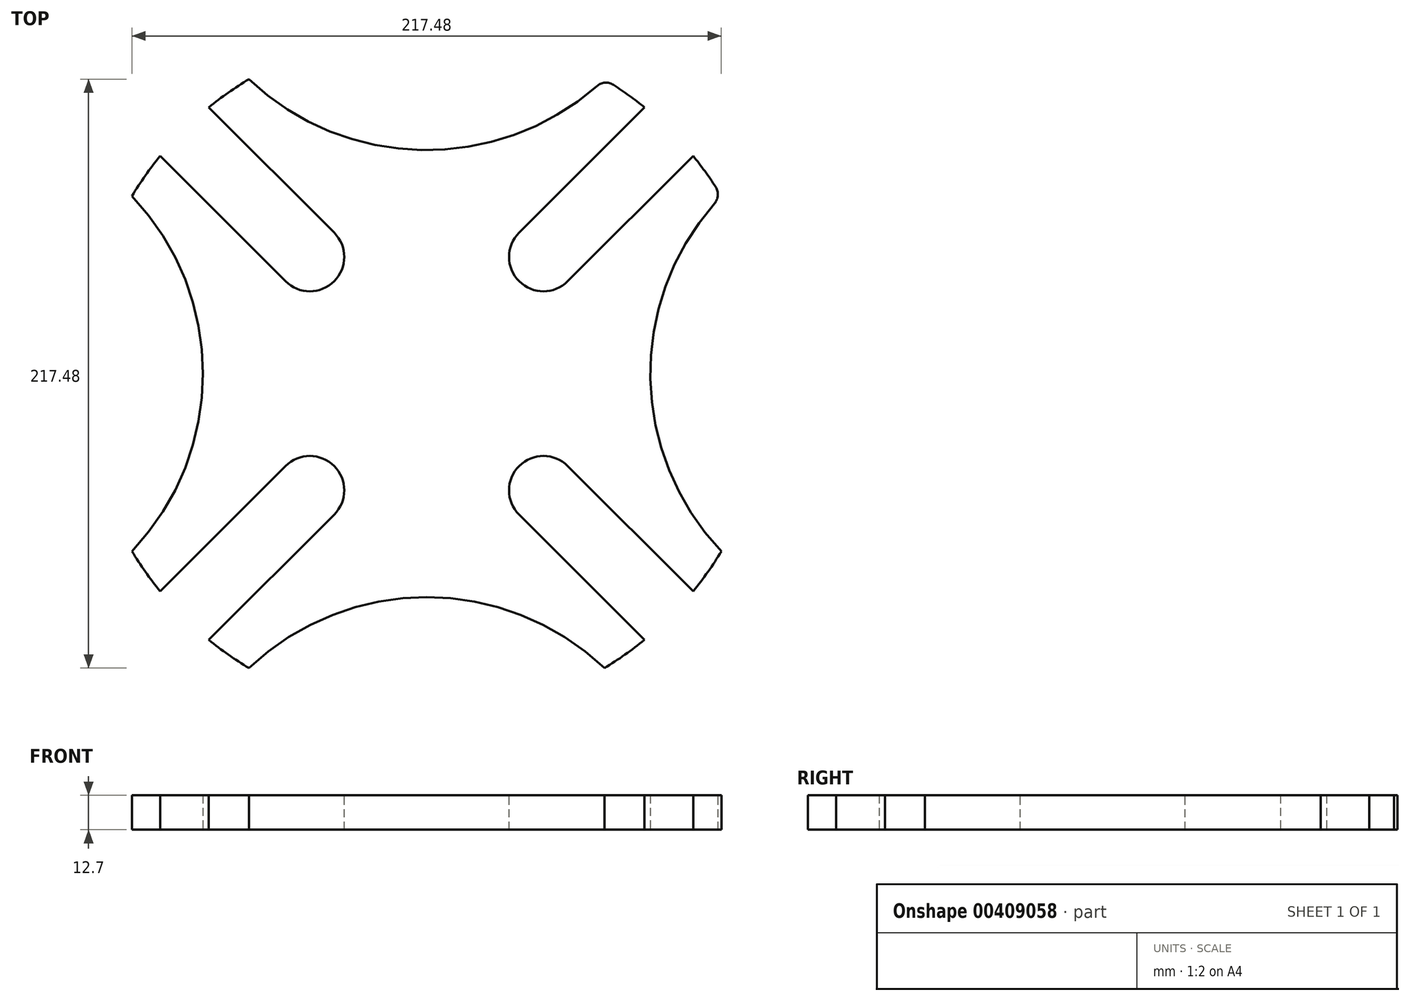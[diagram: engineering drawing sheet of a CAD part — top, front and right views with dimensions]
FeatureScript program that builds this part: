
annotation { "Feature Type Name" : "Feature", "Feature Type Description" : "" }
export const myFeature = defineFeature(function(context is Context, id is Id, definition is map)
    precondition{}
    {
        {
            var Q0;
            Q0=qCreatedBy(makeId("Top.planeOp"),FACE);
            var sketch = newSketch(context, id + "F0", { "sketchPlane" : qUnion([Q0])});
            skArc(sketch, "E0", {"start": v(108.74, 65.6) * mm, "mid": v(89.8, 89.8) * mm, "end": v(65.6, 108.74) * mm});
            skLineSegment(sketch, "E1", {"start": v(0, 0) * mm, "end": v(177.8, 0) * mm, "construction": true});
            skLineSegment(sketch, "E2", {"start": v(0, 0) * mm, "end": v(0, 177.8) * mm, "construction": true});
            skArc(sketch, "E3", {"start": v(108.74, 65.6) * mm, "mid": v(82.55, 0) * mm, "end": v(108.74, -65.6) * mm});
            skArc(sketch, "E4", {"start": v(-65.6, 108.74) * mm, "mid": v(0, 82.55) * mm, "end": v(65.6, 108.74) * mm});
            skArc(sketch, "E5.trimOffspring", {"start": v(-65.6, 108.74) * mm, "mid": v(-89.8, 89.8) * mm, "end": v(-108.74, 65.6) * mm});
            skLineSegment(sketch, "E6", {"start": v(0, 0) * mm, "end": v(-177.8, 0) * mm, "construction": true});
            skLineSegment(sketch, "E7", {"start": v(0, 0) * mm, "end": v(0, -177.8) * mm, "construction": true});
            skArc(sketch, "E8", {"start": v(-108.74, -65.6) * mm, "mid": v(-82.55, 0) * mm, "end": v(-108.74, 65.6) * mm});
            skArc(sketch, "E9", {"start": v(65.6, -108.74) * mm, "mid": v(0, -82.55) * mm, "end": v(-65.6, -108.74) * mm});
            skArc(sketch, "E10.trimOffspring", {"start": v(-108.74, -65.6) * mm, "mid": v(-89.8, -89.8) * mm, "end": v(-65.6, -108.74) * mm});
            skArc(sketch, "E11.trimOffspring", {"start": v(65.6, -108.74) * mm, "mid": v(89.8, -89.8) * mm, "end": v(108.74, -65.6) * mm});
            skSolve(sketch);
        }
        {
            var Q0;
            Q0=makeQuery(id+"F0.imprint","IMPRINT",FACE,{"disambiguationData":[TD([[makeQuery(id+"F0.imprint","IMPRINT",EDGE,{"derivedFrom":sQuery(id+"F0.wireOp",EDGE,"E0")}),1.0]])]});
            extrude(context, id + "F1", {"entities" : qUnion([Q0]), "depth" : 12.7 * mm});
        }
        {
            var Q0;
            Q0=makeQuery(id+"F1.opExtrude","CAP_FACE",FACE,{"disambiguationData":[OSD([sQuery(id+"F0.wireOp",EDGE,"E0"),sQuery(id+"F0.wireOp",EDGE,"E3"),sQuery(id+"F0.wireOp",EDGE,"E4"),sQuery(id+"F0.wireOp",EDGE,"E5.trimOffspring"),sQuery(id+"F0.wireOp",EDGE,"E8"),sQuery(id+"F0.wireOp",EDGE,"E9"),sQuery(id+"F0.wireOp",EDGE,"E10.trimOffspring"),sQuery(id+"F0.wireOp",EDGE,"E11.trimOffspring")])],"isStart":false});
            var sketch = newSketch(context, id + "F2", { "sketchPlane" : qUnion([Q0])});
            skLineSegment(sketch, "E12", {"start": v(0, 0) * mm, "end": v(127, 0) * mm, "construction": true});
            skLineSegment(sketch, "E13", {"start": v(0, 0) * mm, "end": v(96.99, 96.99) * mm, "construction": true});
            skLineSegment(sketch, "E14", {"start": v(96.99, 96.99) * mm, "end": v(105.97, 88) * mm});
            skLineSegment(sketch, "E15", {"start": v(105.97, 88) * mm, "end": v(52.09, 34.12) * mm});
            skLineSegment(sketch, "E16", {"start": v(96.99, 96.99) * mm, "end": v(88, 105.97) * mm});
            skLineSegment(sketch, "E17", {"start": v(88, 105.97) * mm, "end": v(34.12, 52.09) * mm});
            skArc(sketch, "E18", {"start": v(34.12, 52.09) * mm, "mid": v(34.12, 34.12) * mm, "end": v(52.09, 34.12) * mm});
            skArc(sketch, "E19.MirrorCS", {"start": v(-34.12, 52.09) * mm, "mid": v(-34.12, 34.12) * mm, "end": v(-52.09, 34.12) * mm});
            skLineSegment(sketch, "E20.MirrorCS", {"start": v(-88, 105.97) * mm, "end": v(-34.12, 52.09) * mm});
            skLineSegment(sketch, "E21.MirrorCS", {"start": v(-105.97, 88) * mm, "end": v(-52.09, 34.12) * mm});
            skLineSegment(sketch, "E22.MirrorCS", {"start": v(-96.99, 96.99) * mm, "end": v(-105.97, 88) * mm});
            skLineSegment(sketch, "E23.MirrorCS", {"start": v(-96.99, 96.99) * mm, "end": v(-88, 105.97) * mm});
            skArc(sketch, "E24.MirrorCS", {"start": v(-34.12, -52.09) * mm, "mid": v(-34.12, -34.12) * mm, "end": v(-52.09, -34.12) * mm});
            skLineSegment(sketch, "E25.MirrorCS", {"start": v(-88, -105.97) * mm, "end": v(-34.12, -52.09) * mm});
            skLineSegment(sketch, "E26.MirrorCS", {"start": v(-105.97, -88) * mm, "end": v(-52.09, -34.12) * mm});
            skLineSegment(sketch, "E27.MirrorCS", {"start": v(-96.99, -96.99) * mm, "end": v(-105.97, -88) * mm});
            skLineSegment(sketch, "E28.MirrorCS", {"start": v(-96.99, -96.99) * mm, "end": v(-88, -105.97) * mm});
            skLineSegment(sketch, "E29.MirrorCS", {"start": v(88, -105.97) * mm, "end": v(34.12, -52.09) * mm});
            skArc(sketch, "E30.MirrorCS", {"start": v(34.12, -52.09) * mm, "mid": v(34.12, -34.12) * mm, "end": v(52.09, -34.12) * mm});
            skLineSegment(sketch, "E31.MirrorCS", {"start": v(105.97, -88) * mm, "end": v(52.09, -34.12) * mm});
            skLineSegment(sketch, "E32.MirrorCS", {"start": v(96.99, -96.99) * mm, "end": v(105.97, -88) * mm});
            skLineSegment(sketch, "E33.MirrorCS", {"start": v(96.99, -96.99) * mm, "end": v(88, -105.97) * mm});
            skSolve(sketch);
        }
        {
            var Q0;
            Q0=makeQuery(id+"FA7hRxSrrwM2jY9_1.boolean.opBoolean","COPY",EDGE,{"derivedFrom":makeQuery(id+"FA7hRxSrrwM2jY9_1.opExtrude","SWEPT_EDGE",EDGE,{"disambiguationData":[OSD([sQuery(id+"F0.wireOp",EDGE,"E0"),sQuery(id+"F2.wireOp",EDGE,"E15")])]})});
            var Q1;
            Q1=makeQuery(id+"F1.opExtrude","SWEPT_EDGE",EDGE,{"disambiguationData":[OSD([sQuery(id+"F0.wireOp",EDGE,"E0"),sQuery(id+"F0.wireOp",EDGE,"E4")])]});
            var Q2;
            Q2=makeQuery(id+"F1.opExtrude","SWEPT_EDGE",EDGE,{"disambiguationData":[OSD([sQuery(id+"F0.wireOp",EDGE,"E0"),sQuery(id+"F0.wireOp",EDGE,"E3")])]});
            var Q3;
            Q3=makeQuery(id+"FA7hRxSrrwM2jY9_1.boolean.opBoolean","COPY",EDGE,{"derivedFrom":makeQuery(id+"FA7hRxSrrwM2jY9_1.opExtrude","SWEPT_EDGE",EDGE,{"disambiguationData":[OSD([sQuery(id+"F0.wireOp",EDGE,"E0"),sQuery(id+"F2.wireOp",EDGE,"E17")])]})});
            fillet(context, id + "F3", {"entities" : qUnion([Q0, Q1, Q2, Q3]), "radius" : 5.08 * mm, "tangentPropagation" : true, "allowEdgeOverflow" : false});
        }
        {
            var Q0;
            Q0 = qSketchRegion(id + "F2", true);
            extrude(context, id + "F4", {"entities" : qUnion([Q0]), "operationType" : NewBodyOperationType.REMOVE, "oppositeDirection" : true, "depth" : 25.4 * mm});
        }
    });
